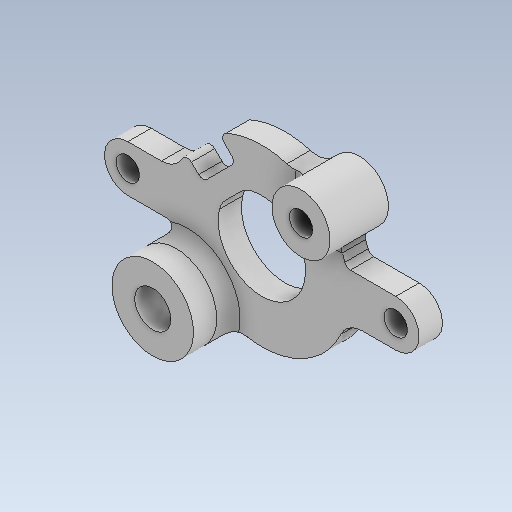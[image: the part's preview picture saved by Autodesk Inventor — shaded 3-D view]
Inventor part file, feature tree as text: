
AUTODESK INVENTOR PART (.ipt)
format: ipt  version: 2023 (Build 270158000, 158)  size: 409,088 bytes
history: native  units: mm
features: fillet x6, extrude x5, sketch x5, reference x5, projected_geometry x5, other x5, chamfer x1
ambient origin geometry x8: Origin, YZ Plane, XZ Plane, XY Plane, X Axis, Y Axis, Z Axis, Center Point
bodies: Solid1 (feature_tree)
feature tree (32):
  extrude  "Extrusion1"  Depth=4.0mm
  extrude  "Extrusion2"  Depth=4.0mm
  fillet  "Fillet1"  Radius=7.5mm
  fillet  "Fillet2"  Radius=9.0mm
  fillet  "Fillet3"  Radius=9.0mm
  fillet  "Fillet4"  Radius=15.0mm
  extrude  "Extrusion3"  Depth=7.0mm
  fillet  "Fillet5"  Radius=4.0mm
  extrude  "Extrusion4"  Depth=7.0mm
  extrude  "Extrusion5"  Depth=2.0mm TaperAngle=0.0deg
  chamfer  "Chamfer1"  Distance=0.5mm
  fillet  "Fillet6"  Radius=2.0mm
  sketch  "Sketch1"  dims[d0=4.0mm d1=4.0mm]
  reference  "Reference1"
  reference  "Reference2"
  reference  "Reference3"
  reference  "Reference4"
  sketch  "Sketch2"  dims[d2=4.8mm d3=4.0mm d4=7.5mm d5=9.0mm d6=9.0mm d7=15.0mm]
  projected_geometry  "Projected Loop1"
  reference  "Reference5"
  sketch  "Sketch3"  dims[d8=5.0mm d9=7.0mm d10=4.0mm]
  projected_geometry  "Projected Loop2"
  sketch  "Sketch4"  dims[d11=5.0mm d12=7.0mm]
  projected_geometry  "Projected Loop3"
  projected_geometry  "Projected Loop4"
  sketch  "Sketch5"  dims[d13=2.0mm d14=0.0mm d15=2.0mm d16=0.0mm d17=0.5mm d18=2.0mm d19=2.0mm d20=0.5mm d21=5.0mm d22=7.0mm d23=3.0mm d24=0.0mm d25=1.0mm d26=3.1mm d27=2.0mm d28=3.0mm d29=0.0mm d30=1.0mm d31=0.0mm d32=1.0mm d33=2.0mm d34=45.0deg d35=1.0mm]
  projected_geometry  "Projected Loop5"
  parser-record x1  (decoder bookkeeping rows leaked as tree rows — omitted from the tree; the rows remain in map.json)
  other  "reducer_1.iam"
  other  "mot_holder_1:1"
  other  "mot_27_ass:1"
  other  "mot_27_2:1"
note: 1 file-system path scrubbed to <path> (originals preserved in map.json)
